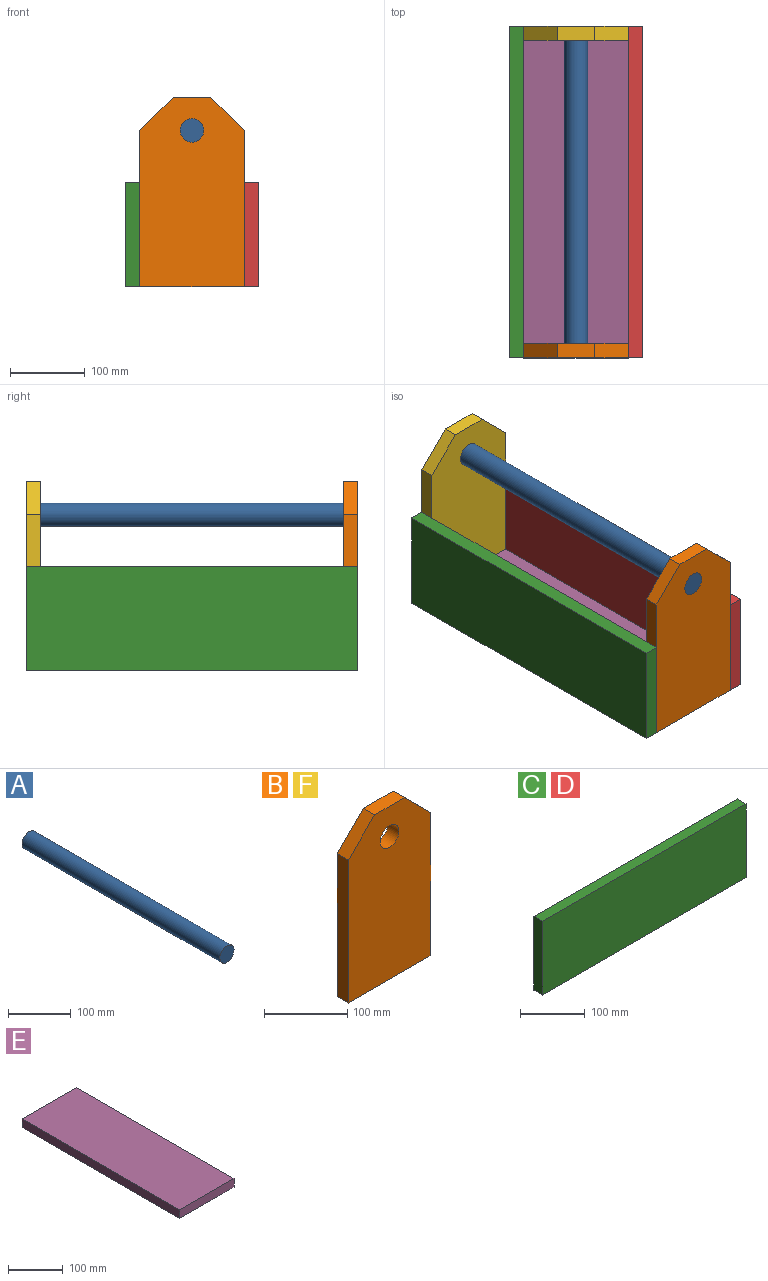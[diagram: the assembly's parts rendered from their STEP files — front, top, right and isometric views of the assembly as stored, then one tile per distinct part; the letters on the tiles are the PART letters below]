
ASSEMBLY  parts=6 mates=5
PART A: 3 faces, bbox 31.8x444.5x31.8 mm
  f0: cylinder r=15.88mm len=444.5mm, axis (0,1,0), area 44336.9mm2, adj f1,f2
  f1: plane 31.75x31.75mm, normal (0,-1,0), area 791.7mm2, adj f0
  f2: plane 31.75x31.75mm, normal (0,1,0), area 791.7mm2, adj f0
PART B: 9 faces, bbox 139.7x19.1x254 mm
  f0: plane 209.55x19.05mm, normal (-1,0,0), area 3991.9mm2, adj f1,f6,f7,f8
  f1: plane 139.7x19.05mm, normal (0,0,-1), area 2661.3mm2, adj f0,f2,f7,f8
  f2: plane 209.55x19.05mm, normal (1,0,0), area 3991.9mm2, adj f1,f3,f7,f8
  f3: plane 44.45x44.45mm, normal (0.71,0,0.71), area 1197.5mm2, adj f2,f4,f7,f8
  f4: plane 50.8x19.05mm, normal (0,0,1), area 967.7mm2, adj f3,f6,f7,f8
  f5: cylinder r=15.88mm len=31.75mm, axis (0,1,0), area 1900.2mm2, adj f7,f8
  f6: plane 44.45x44.45mm, normal (-0.71,0,0.71), area 1197.5mm2, adj f0,f4,f7,f8
  f7: plane 254x139.7mm, normal (0,-1,0), area 32716.3mm2, adj f0,f1,f2,f3,f4,f5,f6
  f8: plane 254x139.7mm, normal (0,1,0), area 32716.3mm2, adj f0,f1,f2,f3,f4,f5,f6
PART C: 6 faces, bbox 444.5x19.1x139.7 mm
  f0: plane 139.7x19.05mm, normal (-1,0,0), area 2661.3mm2, adj f1,f3,f4,f5
  f1: plane 444.5x19.05mm, normal (0,0,-1), area 8467.7mm2, adj f0,f2,f4,f5
  f2: plane 139.7x19.05mm, normal (1,0,0), area 2661.3mm2, adj f1,f3,f4,f5
  f3: plane 444.5x19.05mm, normal (0,0,1), area 8467.7mm2, adj f0,f2,f4,f5
  f4: plane 444.5x139.7mm, normal (0,-1,0), area 62096.6mm2, adj f0,f1,f2,f3
  f5: plane 444.5x139.7mm, normal (0,1,0), area 62096.6mm2, adj f0,f1,f2,f3
PART D: same geometry as C
PART E: 6 faces, bbox 139.7x406.4x19.1 mm
  f0: plane 139.7x19.05mm, normal (0,1,0), area 2661.3mm2, adj f1,f3,f4,f5
  f1: plane 406.4x19.05mm, normal (-1,0,0), area 7741.9mm2, adj f0,f2,f4,f5
  f2: plane 139.7x19.05mm, normal (0,-1,0), area 2661.3mm2, adj f1,f3,f4,f5
  f3: plane 406.4x19.05mm, normal (1,0,0), area 7741.9mm2, adj f0,f2,f4,f5
  f4: plane 406.4x139.7mm, normal (0,0,1), area 56774.1mm2, adj f0,f1,f2,f3
  f5: plane 406.4x139.7mm, normal (0,0,-1), area 56774.1mm2, adj f0,f1,f2,f3
PART F: same geometry as B
PLACE A t=(-107.3,-19.93,342.07)mm
PLACE B t=(-107.3,-223.13,132.52)mm
PLACE C rot(axis=(0,0,-1),90deg) t=(-177.15,-19.93,132.52)mm
PLACE D rot(axis=(0,0,1),90deg) t=(-37.45,-19.93,132.52)mm
PLACE E t=(-107.3,-19.93,132.52)mm
PLACE F rot(axis=(0,0,1),180deg) t=(-107.3,183.27,132.52)mm
MATE fastened F.f8 <-> E.f0  axis (0,-1,0) through (-107.3,183.27,132.52)mm
MATE fastened D.f5 <-> E.f3  axis (-1,0,0) through (-37.45,-19.93,132.52)mm
MATE fastened A.f0 <-> B.f5  axis (0,-1,0) through (-107.3,-242.18,342.07)mm
MATE fastened C.f5 <-> E.f1  axis (1,0,0) through (-177.15,-19.93,132.52)mm
MATE fastened B.f8 <-> E.f2  axis (0,1,0) through (-107.3,-223.13,132.52)mm
